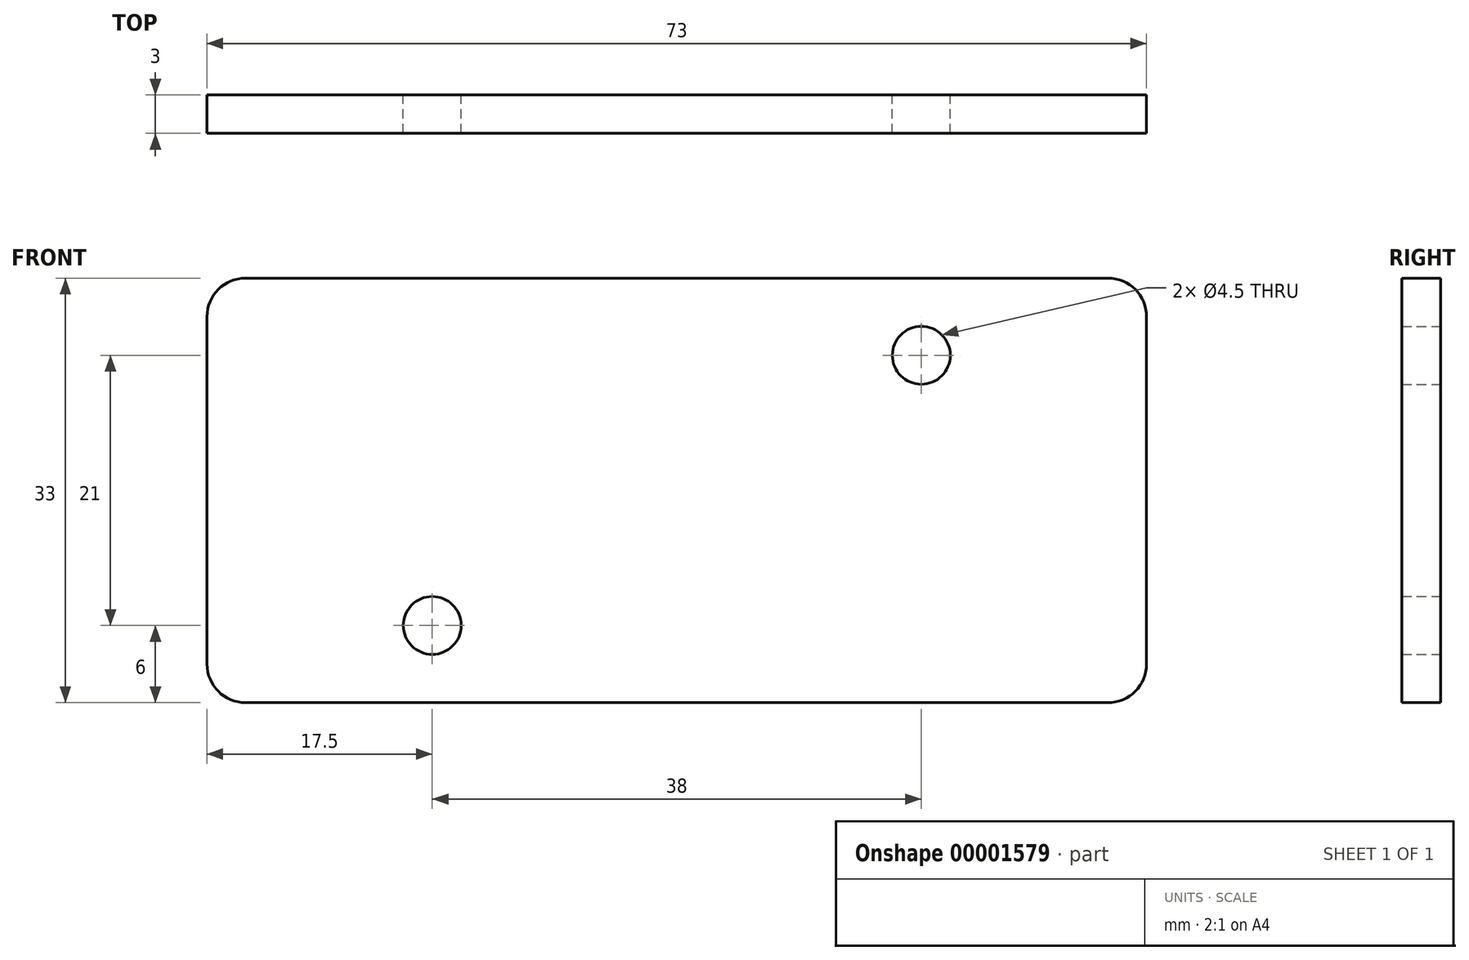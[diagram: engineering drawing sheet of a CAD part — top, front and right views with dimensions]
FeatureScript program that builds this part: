
annotation { "Feature Type Name" : "Feature", "Feature Type Description" : "" }
export const myFeature = defineFeature(function(context is Context, id is Id, definition is map)
    precondition{}
    {
        {
            var Q0;
            Q0=qCreatedBy(makeId("Front.planeOp"),FACE);
            var sketch = newSketch(context, id + "F0", { "sketchPlane" : qUnion([Q0])});
            skCircle(sketch, "E0", {"center": v(0, 0) * mm, "radius": 11.05 * mm, "construction": true});
            skLineSegment(sketch, "E1", {"start": v(0, 0) * mm, "end": v(20.75, 0) * mm, "construction": true});
            skLineSegment(sketch, "E2", {"start": v(0, 10.5) * mm, "end": v(0, -10.5) * mm, "construction": true});
            skLineSegment(sketch, "E3.0.MirrorCS", {"start": v(0, 0) * mm, "end": v(-20.75, 0) * mm, "construction": true});
            skLineSegment(sketch, "E4", {"start": v(0, 10.5) * mm, "end": v(19, 10.5) * mm, "construction": true});
            skCircle(sketch, "E5", {"center": v(19, 10.5) * mm, "radius": 2.25 * mm});
            skLineSegment(sketch, "E6", {"start": v(0, -10.5) * mm, "end": v(-19, -10.5) * mm, "construction": true});
            skCircle(sketch, "E7", {"center": v(-19, -10.5) * mm, "radius": 2.25 * mm});
            skLineSegment(sketch, "E8.rect.bottom", {"start": v(33.5, -16.5) * mm, "end": v(-33.5, -16.5) * mm});
            skLineSegment(sketch, "E8.rect.top", {"start": v(33.5, 16.5) * mm, "end": v(-33.5, 16.5) * mm});
            skLineSegment(sketch, "E8.rect.left", {"start": v(36.5, -13.5) * mm, "end": v(36.5, 13.5) * mm});
            skLineSegment(sketch, "E8.rect.right", {"start": v(-36.5, -13.5) * mm, "end": v(-36.5, 13.5) * mm});
            skPoint(sketch, "E9.visualSharp", {"position": v(-36.5, 16.5) * mm});
            skArc(sketch, "E9.filletArc", {"start": v(-33.5, 16.5) * mm, "mid": v(-35.62, 15.62) * mm, "end": v(-36.5, 13.5) * mm});
            skPoint(sketch, "E10.visualSharp", {"position": v(-36.5, -16.5) * mm});
            skArc(sketch, "E10.filletArc", {"start": v(-36.5, -13.5) * mm, "mid": v(-35.62, -15.62) * mm, "end": v(-33.5, -16.5) * mm});
            skPoint(sketch, "E11.visualSharp", {"position": v(36.5, -16.5) * mm});
            skArc(sketch, "E11.filletArc", {"start": v(33.5, -16.5) * mm, "mid": v(35.62, -15.62) * mm, "end": v(36.5, -13.5) * mm});
            skPoint(sketch, "E12.visualSharp", {"position": v(36.5, 16.5) * mm});
            skArc(sketch, "E12.filletArc", {"start": v(36.5, 13.5) * mm, "mid": v(35.62, 15.62) * mm, "end": v(33.5, 16.5) * mm});
            skSolve(sketch);
        }
        {
            var Q0;
            Q0=makeQuery(id+"F0.imprint","IMPRINT",FACE,{"disambiguationData":[TD([[makeQuery(id+"F0.imprint","IMPRINT",EDGE,{"derivedFrom":sQuery(id+"F0.wireOp",EDGE,"E5")}),-1.0]])]});
            extrude(context, id + "F1", {"entities" : qUnion([Q0]), "depth" : 3 * mm});
        }
    });
